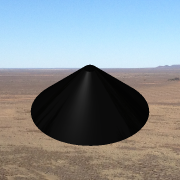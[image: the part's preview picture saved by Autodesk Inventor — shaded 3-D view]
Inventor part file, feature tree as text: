
AUTODESK INVENTOR PART (.ipt)
format: ipt  version: 2013 SP2 (Build 170200200, 200)  size: 152,576 bytes
history: native  units: in
note: dims shown in document units (in); Inventor stores cm internally (conversion verified against a paired STEP export)
features: sketch x2, revolve x1, extrude x1
ambient origin geometry x8: Origin, YZ Plane, XZ Plane, XY Plane, X Axis, Y Axis, Z Axis, Center Point
bodies: Solid1 (feature_tree)
feature tree (4):
  revolve  "Revolution2"  [1 undecoded]
  extrude  "Extrusion3"  [1 undecoded]
  sketch  "Sketch6"  dims[d11=90.0deg d12=1.0in]
  sketch  "Sketch7"  dims[d13=30.0in d14=0.0in]
note: 2 required parameter values undecoded (feature->parameter linkage not recoverable at this tier; creation-order binding heuristic only, values carry confidence <= 0.55)